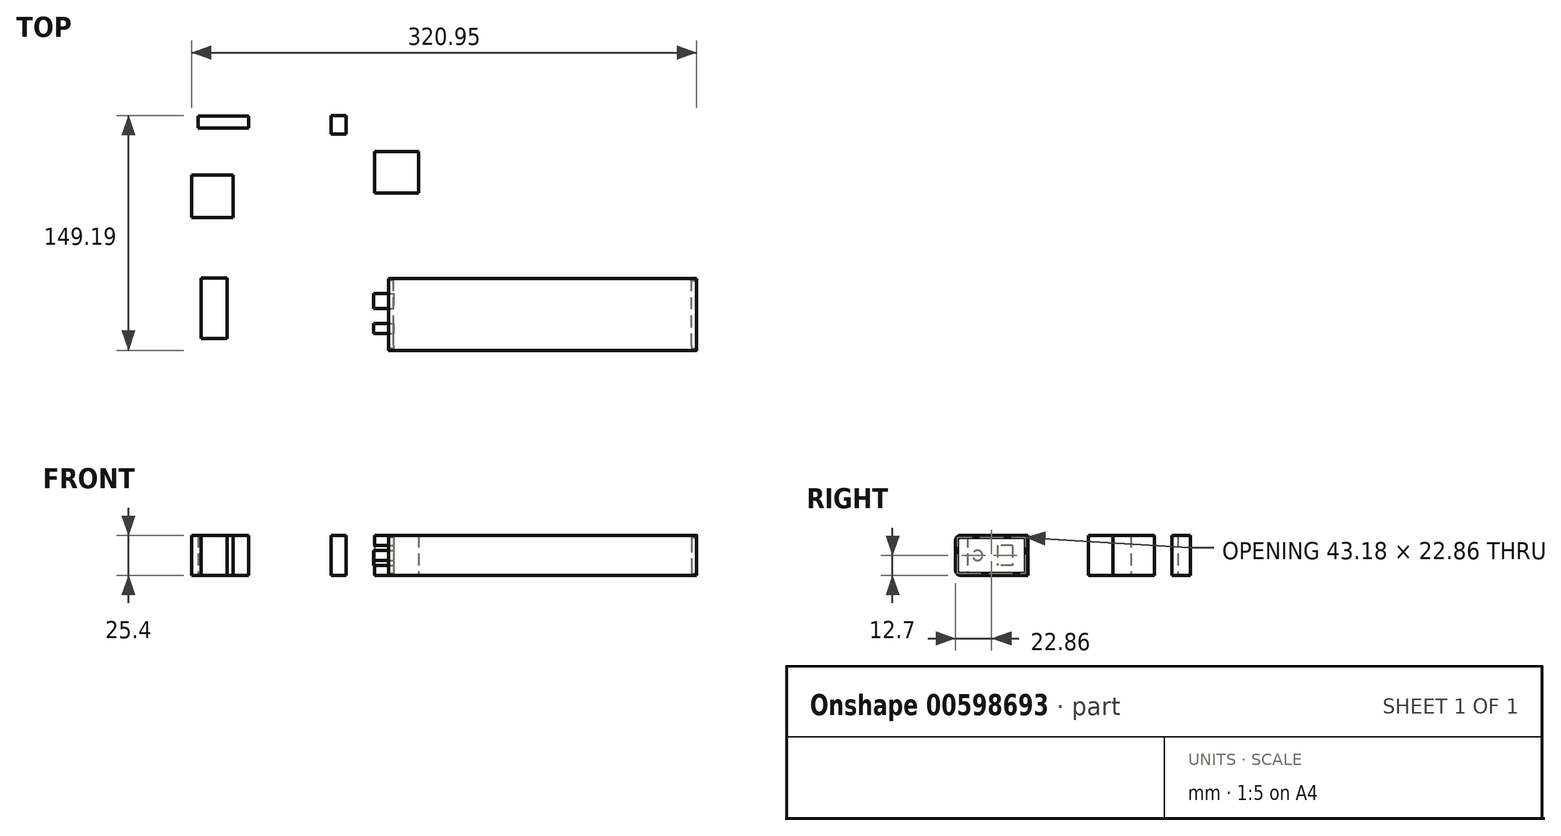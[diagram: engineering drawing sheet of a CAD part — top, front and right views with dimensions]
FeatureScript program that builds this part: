
annotation { "Feature Type Name" : "Feature", "Feature Type Description" : "" }
export const myFeature = defineFeature(function(context is Context, id is Id, definition is map)
    precondition{}
    {
        {
            var Q0;
            Q0=qCreatedBy(makeId("Top.planeOp"),FACE);
            var sketch = newSketch(context, id + "F0", { "sketchPlane" : qUnion([Q0])});
            skLineSegment(sketch, "E0.bottom", {"start": v(-86.43, -67.7) * mm, "end": v(-69.81, -67.7) * mm});
            skLineSegment(sketch, "E0.top", {"start": v(-86.43, -29.2) * mm, "end": v(-69.81, -29.2) * mm});
            skLineSegment(sketch, "E0.left", {"start": v(-86.43, -67.7) * mm, "end": v(-86.43, -29.2) * mm});
            skLineSegment(sketch, "E0.right", {"start": v(-69.81, -67.7) * mm, "end": v(-69.81, -29.2) * mm});
            skLineSegment(sketch, "E1.bottom", {"start": v(-92.45, 9.24) * mm, "end": v(-66.03, 9.24) * mm});
            skLineSegment(sketch, "E1.top", {"start": v(-92.45, 36.24) * mm, "end": v(-66.03, 36.24) * mm});
            skLineSegment(sketch, "E1.left", {"start": v(-92.45, 9.24) * mm, "end": v(-92.45, 36.24) * mm});
            skLineSegment(sketch, "E1.right", {"start": v(-66.03, 9.24) * mm, "end": v(-66.03, 36.24) * mm});
            skLineSegment(sketch, "E2.bottom", {"start": v(-88.14, 65.93) * mm, "end": v(-56, 65.93) * mm});
            skLineSegment(sketch, "E2.top", {"start": v(-88.14, 73.65) * mm, "end": v(-56, 73.65) * mm});
            skLineSegment(sketch, "E2.left", {"start": v(-88.14, 65.93) * mm, "end": v(-88.14, 73.65) * mm});
            skLineSegment(sketch, "E2.right", {"start": v(-56, 65.93) * mm, "end": v(-56, 73.65) * mm});
            skLineSegment(sketch, "E3.bottom", {"start": v(-3.79, 73.98) * mm, "end": v(5.68, 73.98) * mm});
            skLineSegment(sketch, "E3.top", {"start": v(-3.79, 62.28) * mm, "end": v(5.68, 62.28) * mm});
            skLineSegment(sketch, "E3.left", {"start": v(-3.79, 73.98) * mm, "end": v(-3.79, 62.28) * mm});
            skLineSegment(sketch, "E3.right", {"start": v(5.68, 73.98) * mm, "end": v(5.68, 62.28) * mm});
            skLineSegment(sketch, "E4.bottom", {"start": v(23.87, 51.1) * mm, "end": v(51.75, 51.1) * mm});
            skLineSegment(sketch, "E4.top", {"start": v(23.87, 24.73) * mm, "end": v(51.75, 24.73) * mm});
            skLineSegment(sketch, "E4.left", {"start": v(23.87, 51.1) * mm, "end": v(23.87, 24.73) * mm});
            skLineSegment(sketch, "E4.right", {"start": v(51.75, 51.1) * mm, "end": v(51.75, 24.73) * mm});
            skLineSegment(sketch, "E5.bottom", {"start": v(32.92, -29.49) * mm, "end": v(228.5, -29.49) * mm});
            skLineSegment(sketch, "E5.top", {"start": v(32.92, -75.2) * mm, "end": v(228.5, -75.2) * mm});
            skLineSegment(sketch, "E5.left", {"start": v(32.92, -29.49) * mm, "end": v(32.92, -75.2) * mm});
            skLineSegment(sketch, "E5.right", {"start": v(228.5, -29.49) * mm, "end": v(228.5, -75.2) * mm});
            skSolve(sketch);
        }
        {
            var Q0;
            Q0 = qSketchRegion(id + "F0", true);
            extrude(context, id + "F1", {"entities" : qUnion([Q0]), "depth" : 25.4 * mm, "offsetDistance" : 25.4 * mm});
        }
        {
            var Q0;
            Q0=makeQuery(id+"F1.opExtrude","CAP_EDGE",EDGE,{"disambiguationData":[OSD([sQuery(id+"F0.wireOp",EDGE,"E5.top")])],"isStart":false});
            var Q1;
            Q1=makeQuery(id+"F1.opExtrude","CAP_EDGE",EDGE,{"disambiguationData":[OSD([sQuery(id+"F0.wireOp",EDGE,"E5.top")])],"isStart":true});
            var Q2;
            Q2=makeQuery(id+"F1.opExtrude","CAP_EDGE",EDGE,{"disambiguationData":[OSD([sQuery(id+"F0.wireOp",EDGE,"E5.bottom")])],"isStart":true});
            var Q3;
            Q3=makeQuery(id+"F1.opExtrude","CAP_EDGE",EDGE,{"disambiguationData":[OSD([sQuery(id+"F0.wireOp",EDGE,"E5.bottom")])],"isStart":false});
            fillet(context, id + "F2", {"entities" : qUnion([Q0, Q1, Q2, Q3]), "radius" : 3.17 * mm, "tangentPropagation" : true, "allowEdgeOverflow" : false});
        }
        {
            var Q0;
            Q0=makeQuery(id+"F1.opExtrude","SWEPT_FACE",FACE,{"disambiguationData":[OSD([sQuery(id+"F0.wireOp",EDGE,"E5.right")])]});
            var sketch = newSketch(context, id + "F3", { "sketchPlane" : qUnion([Q0])});
            skCircle(sketch, "E6", {"center": v(-72.03, 22.23) * mm, "radius": 1.9 * mm});
            skCircle(sketch, "E7", {"center": v(-32.66, 22.23) * mm, "radius": 1.9 * mm});
            skCircle(sketch, "E8", {"center": v(-72.03, 3.18) * mm, "radius": 1.9 * mm});
            skCircle(sketch, "E9", {"center": v(-32.66, 3.18) * mm, "radius": 1.9 * mm});
            skLineSegment(sketch, "E10", {"start": v(-73.94, 22.23) * mm, "end": v(-73.94, 3.18) * mm});
            skLineSegment(sketch, "E11", {"start": v(-72.03, 1.27) * mm, "end": v(-32.66, 1.27) * mm});
            skLineSegment(sketch, "E12", {"start": v(-30.76, 3.18) * mm, "end": v(-30.76, 22.23) * mm});
            skLineSegment(sketch, "E13", {"start": v(-32.66, 24.13) * mm, "end": v(-72.03, 24.13) * mm});
            skSolve(sketch);
        }
        {
            var Q0;
            Q0 = qSketchRegion(id + "F3", true);
            extrude(context, id + "F4", {"entities" : qUnion([Q0]), "operationType" : NewBodyOperationType.REMOVE, "oppositeDirection" : true, "depth" : 3.17 * mm, "offsetDistance" : 25.4 * mm});
        }
        {
            var Q0;
            Q0=makeQuery(id+"F1.opExtrude","SWEPT_FACE",FACE,{"disambiguationData":[OSD([sQuery(id+"F0.wireOp",EDGE,"E5.left")])]});
            var sketch = newSketch(context, id + "F5", { "sketchPlane" : qUnion([Q0])});
            skCircle(sketch, "E14", {"center": v(32.66, 22.23) * mm, "radius": 1.9 * mm});
            skCircle(sketch, "E15", {"center": v(32.66, 3.18) * mm, "radius": 1.9 * mm});
            skCircle(sketch, "E16", {"center": v(72.03, 3.18) * mm, "radius": 1.9 * mm});
            skCircle(sketch, "E17", {"center": v(72.03, 22.23) * mm, "radius": 1.9 * mm});
            skLineSegment(sketch, "E18", {"start": v(73.94, 3.18) * mm, "end": v(73.94, 22.23) * mm});
            skLineSegment(sketch, "E19", {"start": v(72.03, 24.13) * mm, "end": v(32.66, 24.13) * mm});
            skLineSegment(sketch, "E20", {"start": v(30.76, 22.23) * mm, "end": v(30.76, 3.18) * mm});
            skLineSegment(sketch, "E21", {"start": v(72.03, 1.27) * mm, "end": v(32.66, 1.27) * mm});
            skSolve(sketch);
        }
        {
            var Q0;
            Q0 = qSketchRegion(id + "F5", true);
            extrude(context, id + "F6", {"entities" : qUnion([Q0]), "operationType" : NewBodyOperationType.REMOVE, "oppositeDirection" : true, "depth" : 3.17 * mm, "offsetDistance" : 25.4 * mm});
        }
        {
            var Q0;
            Q0=makeQuery(id+"F6.boolean.opBoolean","COPY",FACE,{"derivedFrom":makeQuery(id+"F6.opExtrude","CAP_FACE",FACE,{"disambiguationData":[OSD([sQuery(id+"F5.wireOp",EDGE,"E14"),sQuery(id+"F5.wireOp",EDGE,"E15"),sQuery(id+"F5.wireOp",EDGE,"E16"),sQuery(id+"F5.wireOp",EDGE,"E17"),sQuery(id+"F5.wireOp",EDGE,"E18"),sQuery(id+"F5.wireOp",EDGE,"E19"),sQuery(id+"F5.wireOp",EDGE,"E20"),sQuery(id+"F5.wireOp",EDGE,"E21")])],"isStart":false})});
            var sketch = newSketch(context, id + "F7", { "sketchPlane" : qUnion([Q0])});
            skLineSegment(sketch, "E22.bottom", {"start": v(39.01, 19.05) * mm, "end": v(48.54, 19.05) * mm});
            skLineSegment(sketch, "E22.top", {"start": v(39.01, 6.35) * mm, "end": v(48.54, 6.35) * mm});
            skLineSegment(sketch, "E22.left", {"start": v(39.01, 19.05) * mm, "end": v(39.01, 6.35) * mm});
            skLineSegment(sketch, "E22.right", {"start": v(48.54, 19.05) * mm, "end": v(48.54, 6.35) * mm});
            skCircle(sketch, "E23", {"center": v(61.24, 12.7) * mm, "radius": 3.18 * mm});
            skPoint(sketch, "E23.centerSnap0", {"position": v(73.94, 12.7) * mm});
            skSolve(sketch);
        }
        {
            var Q0;
            Q0 = qSketchRegion(id + "F7", true);
            extrude(context, id + "F8", {"entities" : qUnion([Q0]), "operationType" : NewBodyOperationType.ADD, "depth" : 12.7 * mm, "offsetDistance" : 25.4 * mm});
        }
    });
